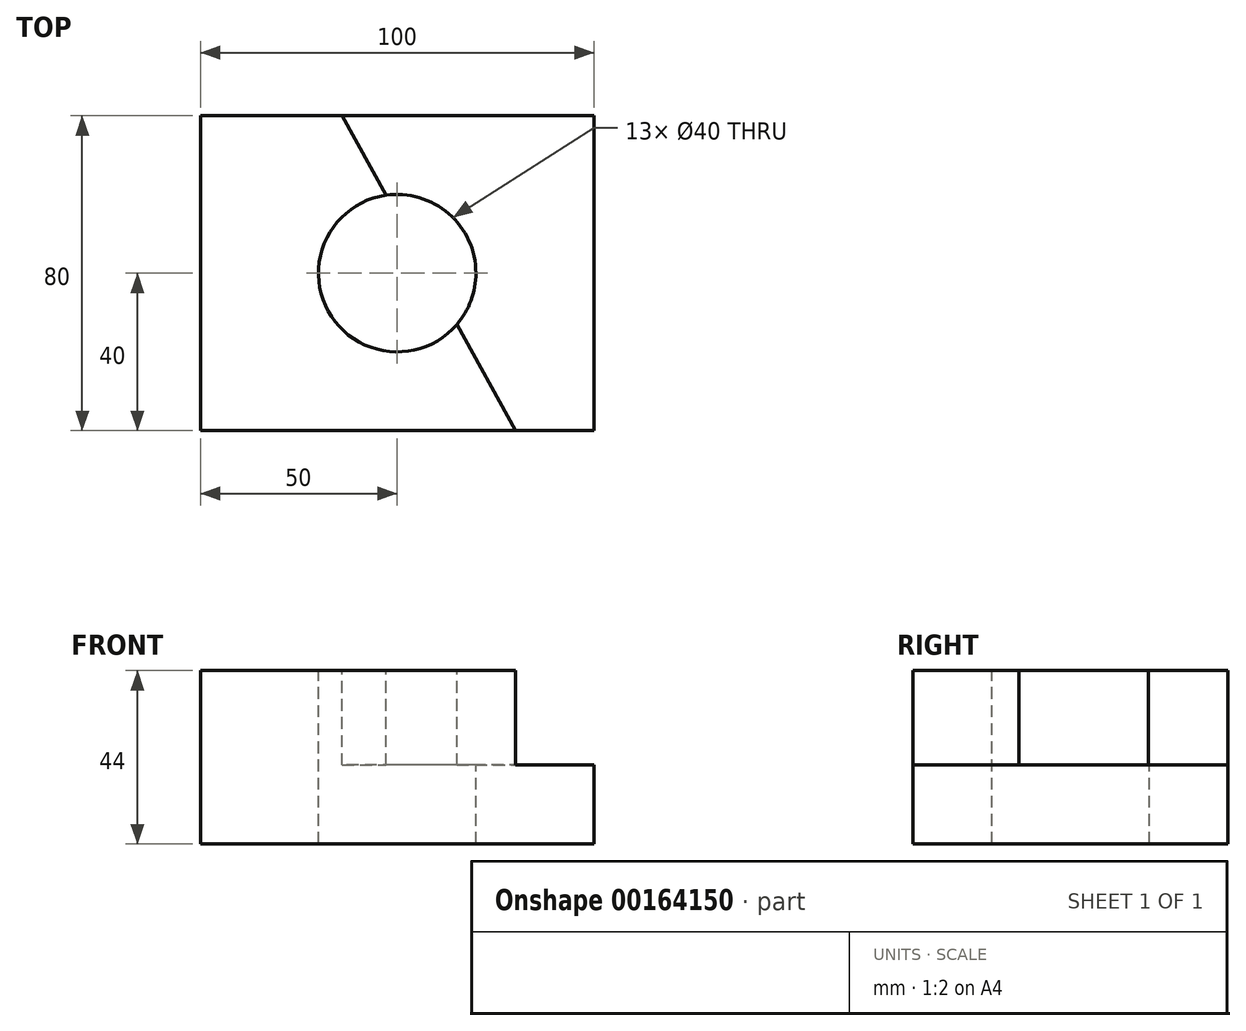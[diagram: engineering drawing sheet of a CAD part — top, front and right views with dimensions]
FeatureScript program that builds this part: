
annotation { "Feature Type Name" : "Feature", "Feature Type Description" : "" }
export const myFeature = defineFeature(function(context is Context, id is Id, definition is map)
    precondition{}
    {
        {
            var Q0;
            Q0=qCreatedBy(makeId("Top.planeOp"),FACE);
            var sketch = newSketch(context, id + "F0", { "sketchPlane" : qUnion([Q0])});
            skLineSegment(sketch, "E0.bottom", {"start": v(50, 40) * mm, "end": v(-50, 40) * mm});
            skLineSegment(sketch, "E0.top", {"start": v(50, -40) * mm, "end": v(-50, -40) * mm});
            skLineSegment(sketch, "E0.left", {"start": v(50, 40) * mm, "end": v(50, -40) * mm});
            skLineSegment(sketch, "E0.right", {"start": v(-50, 40) * mm, "end": v(-50, -40) * mm});
            skPoint(sketch, "E0.middle", {"position": v(0, 0) * mm});
            skSolve(sketch);
        }
        {
            var Q0;
            Q0 = qSketchRegion(id + "F0", true);
            extrude(context, id + "F1", {"entities" : qUnion([Q0]), "depth" : 44 * mm});
        }
        {
            var Q0;
            Q0=makeQuery(id+"F1.opExtrude","CAP_FACE",FACE,{"disambiguationData":[OSD([sQuery(id+"F0.wireOp",EDGE,"E0.bottom"),sQuery(id+"F0.wireOp",EDGE,"E0.top"),sQuery(id+"F0.wireOp",EDGE,"E0.left"),sQuery(id+"F0.wireOp",EDGE,"E0.right")])],"isStart":false});
            var sketch = newSketch(context, id + "F2", { "sketchPlane" : qUnion([Q0])});
            skCircle(sketch, "E1", {"center": v(0, 0) * mm, "radius": 20 * mm});
            skSolve(sketch);
        }
        {
            var Q0;
            Q0=makeQuery(id+"F2.imprint","IMPRINT",FACE,{"disambiguationData":[TD([[makeQuery(id+"F2.imprint","IMPRINT",EDGE,{"derivedFrom":sQuery(id+"F2.wireOp",EDGE,"E1")}),1.0]])]});
            extrude(context, id + "F3", {"entities" : qUnion([Q0]), "operationType" : NewBodyOperationType.REMOVE, "endBound" : BoundingType.THROUGH_ALL, "oppositeDirection" : true, "depth" : 25 * mm});
        }
        {
            var Q0;
            Q0=makeQuery(id+"F1.opExtrude","CAP_FACE",FACE,{"disambiguationData":[OSD([sQuery(id+"F0.wireOp",EDGE,"E0.bottom"),sQuery(id+"F0.wireOp",EDGE,"E0.top"),sQuery(id+"F0.wireOp",EDGE,"E0.left"),sQuery(id+"F0.wireOp",EDGE,"E0.right")])],"isStart":false});
            var sketch = newSketch(context, id + "F4", { "sketchPlane" : qUnion([Q0])});
            skLineSegment(sketch, "E2", {"start": v(-14, 40) * mm, "end": v(30, -40) * mm});
            skLineSegment(sketch, "E3", {"start": v(30, -40) * mm, "end": v(50, -40) * mm});
            skLineSegment(sketch, "E4", {"start": v(50, -40) * mm, "end": v(50, 40) * mm});
            skLineSegment(sketch, "E5", {"start": v(50, 40) * mm, "end": v(-14, 40) * mm});
            skSolve(sketch);
        }
        {
            var Q0;
            {var subQ0=sQuery(id+"F4.wireOp",EDGE,"E3");Q0=makeQuery(id+"F4.imprint","IMPRINT",FACE,{"disambiguationData":[TD([[makeQuery(id+"F4.imprint","IMPRINT",EDGE,{"derivedFrom":subQ0}),-1.0]])]});}
            extrude(context, id + "F5", {"entities" : qUnion([Q0]), "operationType" : NewBodyOperationType.REMOVE, "oppositeDirection" : true, "depth" : 24 * mm});
        }
    });
